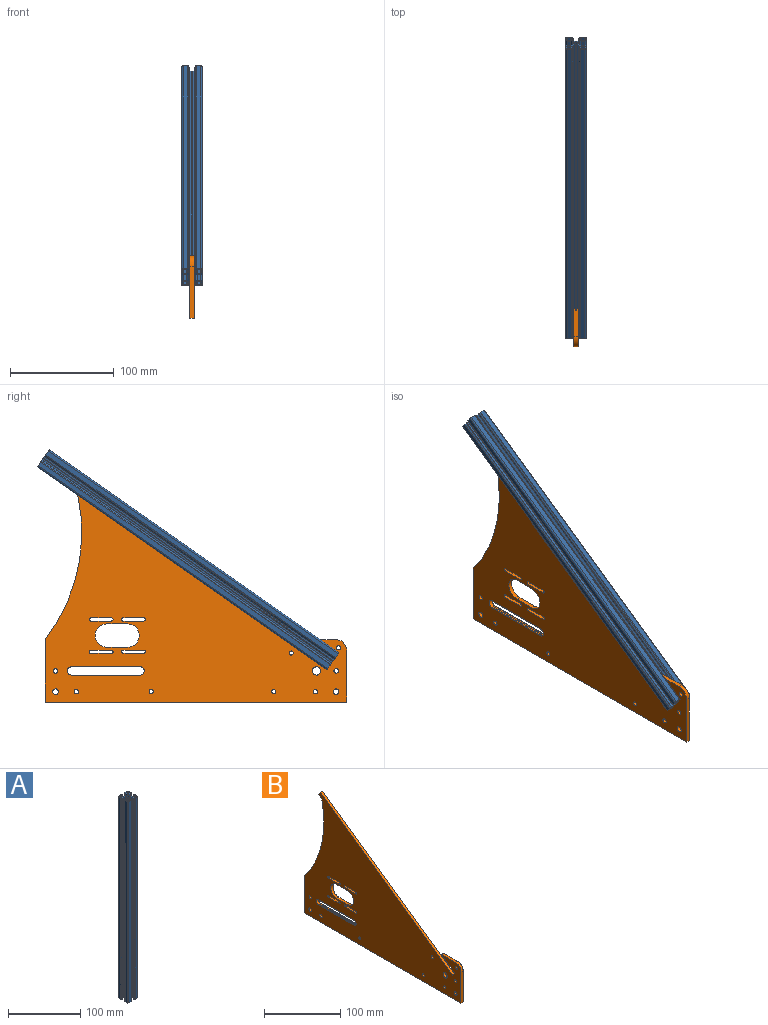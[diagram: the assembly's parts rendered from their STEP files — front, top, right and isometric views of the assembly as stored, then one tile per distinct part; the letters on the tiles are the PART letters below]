
ASSEMBLY  parts=2 mates=1
PART A: 111 faces, bbox 20x20x340 mm
  f0: cylinder r=0.2mm len=340mm, axis (0,0,-1), area 156.7mm2, adj f1,f103,f109,f110
  f1: plane 340x1.28mm, normal (0.71,-0.71,0), area 616.7mm2, adj f0,f2,f109,f110
  f2: cylinder r=0.79mm len=340mm, axis (0,0,-1), area 211mm2, adj f1,f3,f109,f110
  f3: plane 340x4.33mm, normal (1,0,0), area 1472.6mm2, adj f2,f4,f109,f110
  f4: cylinder r=1.5mm len=340mm, axis (0,0,-1), area 741.8mm2, adj f3,f5,f109,f110
  f5: plane 340x4.56mm, normal (0,1,0), area 1548.9mm2, adj f4,f6,f109,f110
  f6: cylinder r=0.8mm len=340mm, axis (0,0,-1), area 213.6mm2, adj f5,f7,f109,f110
  f7: plane 340x1.1mm, normal (-0.71,0.71,0), area 530.8mm2, adj f6,f8,f109,f110
  f8: cylinder r=0.25mm len=340mm, axis (0,0,-1), area 200.3mm2, adj f7,f9,f109,f110
  f9: plane 340x1.05mm, normal (0,-1,0), area 357mm2, adj f8,f10,f109,f110
  f10: plane 340x3.2mm, normal (-1,0,0), area 1088mm2, adj f9,f11,f109,f110
  f11: plane 340x1.6mm, normal (-0.71,0.71,0), area 768mm2, adj f10,f12,f109,f110
  f12: plane 340x1.71mm, normal (0,1,0), area 579.8mm2, adj f11,f13,f109,f110
  f13: plane 340x0.3mm, normal (-0.65,0.76,0), area 135mm2, adj f12,f14,f109,f110
  f14: plane 340x0.3mm, normal (0.65,0.76,0), area 135mm2, adj f13,f15,f109,f110
  f15: plane 340x1.71mm, normal (0,1,0), area 579.8mm2, adj f14,f16,f109,f110
  f16: plane 340x1.6mm, normal (0.71,0.71,0), area 768mm2, adj f15,f17,f109,f110
  f17: plane 340x3.2mm, normal (1,0,0), area 1088mm2, adj f16,f18,f109,f110
  f18: plane 340x1.05mm, normal (0,-1,0), area 357mm2, adj f17,f19,f109,f110
  f19: cylinder r=0.25mm len=340mm, axis (0,0,-1), area 200.3mm2, adj f18,f20,f109,f110
  f20: plane 340x1.1mm, normal (0.71,0.71,0), area 530.8mm2, adj f19,f21,f109,f110
  f21: cylinder r=0.8mm len=340mm, axis (0,0,-1), area 213.6mm2, adj f20,f22,f109,f110
  f22: plane 340x4.56mm, normal (0,1,0), area 1548.9mm2, adj f21,f23,f109,f110
  f23: cylinder r=1.5mm len=340mm, axis (0,0,-1), area 741.8mm2, adj f22,f24,f109,f110
  f24: plane 340x4.33mm, normal (-1,0,0), area 1472.6mm2, adj f23,f25,f109,f110
  f25: cylinder r=0.79mm len=340mm, axis (0,0,-1), area 211mm2, adj f24,f26,f109,f110
  f26: plane 340x1.28mm, normal (-0.71,-0.71,0), area 616.7mm2, adj f25,f27,f109,f110
  f27: cylinder r=0.2mm len=340mm, axis (0,0,-1), area 156.7mm2, adj f26,f28,f109,f110
  f28: plane 340x1.06mm, normal (1,0,0), area 360.5mm2, adj f27,f29,f109,f110
  f29: plane 340x3.12mm, normal (0,-1,0), area 1059.6mm2, adj f28,f30,f109,f110
  f30: plane 340x1.63mm, normal (-0.71,-0.71,0), area 784.3mm2, adj f29,f31,f109,f110
  f31: plane 340x1.59mm, normal (-1,0,0), area 539mm2, adj f30,f32,f109,f110
  f32: plane 340x0.38mm, normal (-0.71,-0.71,0), area 183.1mm2, adj f31,f33,f109,f110
  f33: plane 340x0.38mm, normal (-0.71,0.71,0), area 183.1mm2, adj f32,f34,f109,f110
  f34: plane 340x1.59mm, normal (-1,0,0), area 539mm2, adj f33,f35,f109,f110
  f35: plane 340x1.63mm, normal (-0.71,0.71,0), area 784.3mm2, adj f34,f36,f109,f110
  f36: plane 340x3.12mm, normal (0,1,0), area 1059.6mm2, adj f35,f37,f109,f110
  f37: plane 340x1.06mm, normal (1,0,0), area 360.5mm2, adj f36,f38,f109,f110
  f38: cylinder r=0.2mm len=340mm, axis (0,0,-1), area 156.7mm2, adj f37,f39,f109,f110
  f39: plane 340x1.28mm, normal (-0.71,0.71,0), area 616.7mm2, adj f38,f40,f109,f110
  f40: cylinder r=0.79mm len=340mm, axis (0,0,-1), area 211mm2, adj f39,f41,f109,f110
  f41: plane 340x4.33mm, normal (-1,0,0), area 1472.6mm2, adj f40,f42,f109,f110
  f42: cylinder r=1.5mm len=340mm, axis (0,0,-1), area 741.8mm2, adj f41,f43,f109,f110
  f43: plane 340x4.56mm, normal (0,-1,0), area 1548.9mm2, adj f42,f44,f109,f110
  f44: cylinder r=0.8mm len=340mm, axis (0,0,-1), area 213.6mm2, adj f43,f45,f109,f110
  f45: plane 340x1.1mm, normal (0.71,-0.71,0), area 530.8mm2, adj f44,f46,f109,f110
  f46: cylinder r=0.25mm len=340mm, axis (0,0,-1), area 200.3mm2, adj f45,f47,f109,f110
  f47: plane 340x1.05mm, normal (0,1,0), area 357mm2, adj f46,f48,f109,f110
  f48: plane 340x3.2mm, normal (1,0,0), area 1088mm2, adj f47,f49,f109,f110
  f49: plane 340x1.6mm, normal (0.71,-0.71,0), area 768mm2, adj f48,f50,f109,f110
  f50: plane 340x1.71mm, normal (0,-1,0), area 579.8mm2, adj f49,f51,f109,f110
  f51: plane 340x0.3mm, normal (0.65,-0.76,0), area 135mm2, adj f50,f52,f109,f110
  f52: plane 340x0.3mm, normal (-0.65,-0.76,0), area 135mm2, adj f51,f53,f109,f110
  f53: plane 340x1.71mm, normal (0,-1,0), area 579.8mm2, adj f52,f54,f109,f110
  f54: plane 340x1.6mm, normal (-0.71,-0.71,0), area 768mm2, adj f53,f55,f109,f110
  f55: plane 340x3.2mm, normal (-1,0,0), area 1088mm2, adj f54,f56,f109,f110
  f56: plane 340x1.05mm, normal (0,1,0), area 357mm2, adj f55,f57,f109,f110
  f57: cylinder r=0.25mm len=340mm, axis (0,0,-1), area 200.3mm2, adj f56,f58,f109,f110
  f58: plane 340x1.1mm, normal (-0.71,-0.71,0), area 530.8mm2, adj f57,f59,f109,f110
  f59: cylinder r=0.8mm len=340mm, axis (0,0,-1), area 213.6mm2, adj f58,f60,f109,f110
  f60: plane 340x4.56mm, normal (0,-1,0), area 1548.9mm2, adj f59,f61,f109,f110
  f61: cylinder r=1.5mm len=340mm, axis (0,0,-1), area 741.8mm2, adj f60,f62,f109,f110
  f62: plane 340x4.33mm, normal (1,0,0), area 1472.6mm2, adj f61,f63,f109,f110
  f63: cylinder r=0.79mm len=340mm, axis (0,0,-1), area 211mm2, adj f62,f64,f109,f110
  f64: plane 340x1.28mm, normal (0.71,0.71,0), area 616.7mm2, adj f63,f65,f109,f110
  f65: cylinder r=0.2mm len=340mm, axis (0,0,-1), area 156.7mm2, adj f64,f66,f109,f110
  f66: plane 340x1.06mm, normal (-1,0,0), area 360.5mm2, adj f65,f67,f109,f110
  f67: plane 340x3.12mm, normal (0,1,0), area 1059.6mm2, adj f66,f68,f109,f110
  f68: plane 340x1.63mm, normal (0.71,0.71,0), area 784.3mm2, adj f67,f69,f109,f110
  f69: plane 340x1.59mm, normal (1,0,0), area 539mm2, adj f68,f70,f109,f110
  f70: plane 340x0.38mm, normal (0.71,0.71,0), area 183.1mm2, adj f69,f71,f109,f110
  f71: plane 340x0.38mm, normal (0.71,-0.71,0), area 183.1mm2, adj f70,f72,f109,f110
  f72: plane 340x1.59mm, normal (1,0,0), area 539mm2, adj f71,f73,f109,f110
  f73: plane 340x1.63mm, normal (0.71,-0.71,0), area 784.3mm2, adj f72,f74,f109,f110
  f74: plane 340x3.12mm, normal (0,-1,0), area 1059.6mm2, adj f73,f103,f109,f110
  f75: plane 340x3mm, normal (0,1,0), area 1020mm2, adj f76,f104,f109,f110
  f76: cylinder r=0.5mm len=340mm, axis (0,0,-1), area 210.5mm2, adj f75,f77,f109,f110
  f77: plane 340x3mm, normal (1,0,0), area 1020mm2, adj f76,f78,f109,f110
  f78: cylinder r=0.5mm len=340mm, axis (0,0,-1), area 269.3mm2, adj f77,f79,f109,f110
  f79: plane 340x3mm, normal (0,-1,0), area 1020mm2, adj f78,f80,f109,f110
  f80: cylinder r=0.5mm len=340mm, axis (0,0,-1), area 331.1mm2, adj f79,f81,f109,f110
  f81: plane 340x3mm, normal (-1,0,0), area 1020mm2, adj f80,f104,f109,f110
  f82: plane 340x3mm, normal (0,1,0), area 1020mm2, adj f83,f105,f109,f110
  f83: cylinder r=0.5mm len=340mm, axis (0,0,-1), area 331.1mm2, adj f82,f84,f109,f110
  f84: plane 340x3mm, normal (1,0,0), area 1020mm2, adj f83,f85,f109,f110
  f85: cylinder r=0.5mm len=340mm, axis (0,0,-1), area 278.6mm2, adj f84,f86,f109,f110
  f86: plane 340x3mm, normal (0,-1,0), area 1020mm2, adj f85,f87,f109,f110
  f87: cylinder r=0.5mm len=340mm, axis (0,0,-1), area 210.5mm2, adj f86,f88,f109,f110
  f88: plane 340x3mm, normal (-1,0,0), area 1020mm2, adj f87,f105,f109,f110
  f89: cylinder r=0.5mm len=340mm, axis (0,0,-1), area 278.6mm2, adj f90,f106,f109,f110
  f90: plane 340x3mm, normal (1,0,0), area 1020mm2, adj f89,f91,f109,f110
  f91: cylinder r=0.5mm len=340mm, axis (0,0,-1), area 331.1mm2, adj f90,f92,f109,f110
  f92: plane 340x3mm, normal (0,-1,0), area 1020mm2, adj f91,f93,f109,f110
  f93: cylinder r=0.5mm len=340mm, axis (0,0,-1), area 269.3mm2, adj f92,f94,f109,f110
  f94: plane 340x3mm, normal (-1,0,0), area 1020mm2, adj f93,f95,f109,f110
  f95: cylinder r=0.5mm len=340mm, axis (0,0,-1), area 210.5mm2, adj f94,f106,f109,f110
  f96: cylinder r=0.5mm len=340mm, axis (0,0,-1), area 278.6mm2, adj f97,f107,f109,f110
  f97: plane 340x3mm, normal (-1,0,0), area 1020mm2, adj f96,f98,f109,f110
  f98: cylinder r=0.5mm len=340mm, axis (0,0,-1), area 331.1mm2, adj f97,f99,f109,f110
  f99: plane 340x3mm, normal (0,1,0), area 1020mm2, adj f98,f100,f109,f110
  f100: cylinder r=0.5mm len=340mm, axis (0,0,-1), area 269.3mm2, adj f99,f101,f109,f110
  f101: plane 340x3mm, normal (1,0,0), area 1020mm2, adj f100,f102,f109,f110
  f102: cylinder r=0.5mm len=340mm, axis (0,0,-1), area 210.5mm2, adj f101,f107,f109,f110
  f103: plane 340x1.06mm, normal (-1,0,0), area 360.5mm2, adj f0,f74,f109,f110
  f104: cylinder r=0.5mm len=340mm, axis (0,0,-1), area 278.6mm2, adj f75,f81,f109,f110
  f105: cylinder r=0.5mm len=340mm, axis (0,0,-1), area 269.3mm2, adj f82,f88,f109,f110
  f106: plane 340x3mm, normal (0,1,0), area 1020mm2, adj f89,f95,f109,f110
  f107: plane 340x3mm, normal (0,-1,0), area 1020mm2, adj f96,f102,f109,f110
  f108: cylinder r=2.1mm len=340mm, axis (0,0,-1), area 4486.2mm2, adj f109,f110
  f109: plane 20x20mm, normal (0,0,1), area 150.7mm2, adj f0,f1,f2,f3,f4,f5,f6,f7
  f110: plane 20x20mm, normal (0,0,-1), area 150.7mm2, adj f0,f1,f2,f3,f4,f5,f6,f7
PART B: 176 faces, bbox 4x290x208.7 mm
  f0: cylinder r=1.5mm len=4mm, axis (1,0,0), area 18.8mm2, adj f1,f156,f173,f174
  f1: plane 20x4mm, normal (0,0,-1), area 80mm2, adj f0,f2,f173,f174
  f2: cylinder r=1.5mm len=4mm, axis (1,0,0), area 18.8mm2, adj f1,f156,f173,f174
  f3: plane 20x4mm, normal (0,0,-1), area 80mm2, adj f4,f157,f173,f174
  f4: cylinder r=1.5mm len=4mm, axis (1,0,0), area 18.8mm2, adj f3,f5,f173,f174
  f5: plane 20x4mm, normal (0,0,1), area 80mm2, adj f4,f157,f173,f174
  f6: plane 19.99x4mm, normal (0,0,-1), area 80mm2, adj f7,f158,f173,f174
  f7: cylinder r=1.5mm len=4mm, axis (1,0,0), area 18.8mm2, adj f6,f8,f173,f174
  f8: plane 19.99x4mm, normal (0,0,1), area 80mm2, adj f7,f158,f173,f174
  f9: plane 20x4mm, normal (0,0,-1), area 80mm2, adj f10,f159,f173,f174
  f10: cylinder r=11.2mm len=22.4mm, axis (1,0,0), area 140.7mm2, adj f9,f11,f173,f174
  f11: plane 20x4mm, normal (0,0,1), area 80mm2, adj f10,f159,f173,f174
  f12: cylinder r=1.5mm len=4mm, axis (1,0,0), area 18.9mm2, adj f13,f160,f173,f174
  f13: plane 19.99x4mm, normal (0,0,-1), area 80mm2, adj f12,f14,f173,f174
  f14: cylinder r=1.5mm len=4mm, axis (1,0,0), area 18.8mm2, adj f13,f160,f173,f174
  f15: cylinder r=4mm len=8mm, axis (1,0,0), area 54.3mm2, adj f16,f164,f173,f174
  f16: cylinder r=4mm len=4mm, axis (1,0,0), area 4mm2, adj f15,f17,f173,f174
  f17: cylinder r=4mm len=4mm, axis (1,0,0), area 4mm2, adj f16,f18,f173,f174
  f18: cylinder r=4mm len=4mm, axis (1,0,0), area 4mm2, adj f17,f19,f173,f174
  f19: cylinder r=4mm len=4mm, axis (1,0,0), area 4mm2, adj f18,f20,f173,f174
  f20: cylinder r=4mm len=4mm, axis (1,0,0), area 4mm2, adj f19,f21,f173,f174
  f21: cylinder r=4mm len=4mm, axis (1,0,0), area 4mm2, adj f20,f22,f173,f174
  f22: cylinder r=4mm len=4mm, axis (1,0,0), area 4mm2, adj f21,f23,f173,f174
  f23: cylinder r=4mm len=4mm, axis (1,0,0), area 4mm2, adj f22,f24,f173,f174
  f24: cylinder r=4mm len=4mm, axis (1,0,0), area 4mm2, adj f23,f25,f173,f174
  f25: cylinder r=4mm len=4mm, axis (1,0,0), area 4mm2, adj f24,f26,f173,f174
  f26: cylinder r=4mm len=4mm, axis (1,0,0), area 4mm2, adj f25,f27,f173,f174
  f27: cylinder r=4mm len=4mm, axis (1,0,0), area 4mm2, adj f26,f28,f173,f174
  f28: cylinder r=4mm len=4mm, axis (1,0,0), area 4mm2, adj f27,f29,f173,f174
  f29: cylinder r=4mm len=4mm, axis (1,0,0), area 4mm2, adj f28,f30,f173,f174
  f30: cylinder r=4mm len=4mm, axis (1,0,0), area 4mm2, adj f29,f31,f173,f174
  f31: cylinder r=4mm len=4mm, axis (1,0,0), area 4mm2, adj f30,f32,f173,f174
  f32: cylinder r=4mm len=4mm, axis (1,0,0), area 4mm2, adj f31,f33,f173,f174
  f33: cylinder r=4mm len=4mm, axis (1,0,0), area 4mm2, adj f32,f34,f173,f174
  f34: cylinder r=4mm len=4mm, axis (1,0,0), area 4mm2, adj f33,f35,f173,f174
  f35: cylinder r=4mm len=4mm, axis (1,0,0), area 4mm2, adj f34,f36,f173,f174
  f36: cylinder r=4mm len=4mm, axis (1,0,0), area 4mm2, adj f35,f37,f173,f174
  f37: cylinder r=4mm len=4mm, axis (1,0,0), area 4mm2, adj f36,f38,f173,f174
  f38: cylinder r=4mm len=4mm, axis (1,0,0), area 4mm2, adj f37,f39,f173,f174
  f39: cylinder r=4mm len=4mm, axis (1,0,0), area 4mm2, adj f38,f40,f173,f174
  f40: cylinder r=4mm len=4mm, axis (1,0,0), area 4mm2, adj f39,f41,f173,f174
  f41: cylinder r=4mm len=4mm, axis (1,0,0), area 4mm2, adj f40,f42,f173,f174
  f42: cylinder r=4mm len=4mm, axis (1,0,0), area 4mm2, adj f41,f43,f173,f174
  f43: cylinder r=4mm len=4mm, axis (1,0,0), area 4mm2, adj f42,f44,f173,f174
  f44: cylinder r=4mm len=4mm, axis (1,0,0), area 4mm2, adj f43,f45,f173,f174
  f45: cylinder r=4mm len=4mm, axis (1,0,0), area 4mm2, adj f44,f46,f173,f174
  f46: cylinder r=4mm len=4mm, axis (1,0,0), area 4mm2, adj f45,f47,f173,f174
  f47: cylinder r=4mm len=4mm, axis (1,0,0), area 4mm2, adj f46,f48,f173,f174
  f48: cylinder r=4mm len=4mm, axis (1,0,0), area 4mm2, adj f47,f49,f173,f174
  f49: cylinder r=4mm len=4mm, axis (1,0,0), area 4mm2, adj f48,f50,f173,f174
  f50: cylinder r=4mm len=4mm, axis (1,0,0), area 4mm2, adj f49,f51,f173,f174
  f51: cylinder r=4mm len=4mm, axis (1,0,0), area 4mm2, adj f50,f52,f173,f174
  f52: cylinder r=4mm len=4mm, axis (1,0,0), area 4mm2, adj f51,f53,f173,f174
  f53: cylinder r=4mm len=4mm, axis (1,0,0), area 4mm2, adj f52,f54,f173,f174
  f54: cylinder r=4mm len=4mm, axis (1,0,0), area 4mm2, adj f53,f55,f173,f174
  f55: cylinder r=4mm len=4mm, axis (1,0,0), area 4mm2, adj f54,f56,f173,f174
  f56: cylinder r=4mm len=4mm, axis (1,0,0), area 4mm2, adj f55,f57,f173,f174
  f57: cylinder r=4mm len=4mm, axis (1,0,0), area 4mm2, adj f56,f58,f173,f174
  f58: cylinder r=4mm len=4mm, axis (1,0,0), area 4mm2, adj f57,f59,f173,f174
  f59: cylinder r=4mm len=4mm, axis (1,0,0), area 4mm2, adj f58,f60,f173,f174
  f60: cylinder r=4mm len=4mm, axis (1,0,0), area 4mm2, adj f59,f61,f173,f174
  f61: cylinder r=4mm len=4mm, axis (1,0,0), area 4mm2, adj f60,f62,f173,f174
  f62: cylinder r=4mm len=4mm, axis (1,0,0), area 4mm2, adj f61,f63,f173,f174
  f63: cylinder r=4mm len=4mm, axis (1,0,0), area 4mm2, adj f62,f64,f173,f174
  f64: cylinder r=4mm len=4mm, axis (1,0,0), area 4mm2, adj f63,f65,f173,f174
  f65: cylinder r=4mm len=4mm, axis (1,0,0), area 4mm2, adj f64,f66,f173,f174
  f66: cylinder r=4mm len=4mm, axis (1,0,0), area 4mm2, adj f65,f67,f173,f174
  f67: cylinder r=4mm len=4mm, axis (1,0,0), area 4mm2, adj f66,f68,f173,f174
  f68: cylinder r=4mm len=4mm, axis (1,0,0), area 4mm2, adj f67,f69,f173,f174
  f69: cylinder r=4mm len=4mm, axis (1,0,0), area 4mm2, adj f68,f70,f173,f174
  f70: cylinder r=4mm len=4mm, axis (1,0,0), area 4mm2, adj f69,f71,f173,f174
  f71: cylinder r=4mm len=4mm, axis (1,0,0), area 4mm2, adj f70,f72,f173,f174
  f72: cylinder r=4mm len=4mm, axis (1,0,0), area 4mm2, adj f71,f73,f173,f174
  f73: cylinder r=4mm len=4mm, axis (1,0,0), area 4mm2, adj f72,f74,f173,f174
  f74: cylinder r=4mm len=4mm, axis (1,0,0), area 4mm2, adj f73,f75,f173,f174
  f75: cylinder r=4mm len=4mm, axis (1,0,0), area 4mm2, adj f74,f76,f173,f174
  f76: cylinder r=4mm len=4mm, axis (1,0,0), area 4mm2, adj f75,f77,f173,f174
  f77: cylinder r=4mm len=4mm, axis (1,0,0), area 4mm2, adj f76,f78,f173,f174
  f78: cylinder r=4mm len=4mm, axis (1,0,0), area 4mm2, adj f77,f79,f173,f174
  f79: cylinder r=4mm len=4mm, axis (1,0,0), area 4mm2, adj f78,f80,f173,f174
  f80: cylinder r=4mm len=4mm, axis (1,0,0), area 4mm2, adj f79,f81,f173,f174
  f81: cylinder r=4mm len=8mm, axis (1,0,0), area 54.3mm2, adj f80,f82,f173,f174
  f82: cylinder r=4mm len=4mm, axis (1,0,0), area 4mm2, adj f81,f83,f173,f174
  f83: cylinder r=4mm len=4mm, axis (1,0,0), area 4mm2, adj f82,f84,f173,f174
  f84: cylinder r=4mm len=4mm, axis (1,0,0), area 4mm2, adj f83,f85,f173,f174
  f85: cylinder r=4mm len=4mm, axis (1,0,0), area 4mm2, adj f84,f86,f173,f174
  f86: cylinder r=4mm len=4mm, axis (1,0,0), area 4mm2, adj f85,f87,f173,f174
  f87: cylinder r=4mm len=4mm, axis (1,0,0), area 4mm2, adj f86,f88,f173,f174
  f88: cylinder r=4mm len=4mm, axis (1,0,0), area 4mm2, adj f87,f89,f173,f174
  f89: cylinder r=4mm len=4mm, axis (1,0,0), area 4mm2, adj f88,f90,f173,f174
  f90: cylinder r=4mm len=4mm, axis (1,0,0), area 4mm2, adj f89,f91,f173,f174
  f91: cylinder r=4mm len=4mm, axis (1,0,0), area 4mm2, adj f90,f92,f173,f174
  f92: cylinder r=4mm len=4mm, axis (1,0,0), area 4mm2, adj f91,f93,f173,f174
  f93: cylinder r=4mm len=4mm, axis (1,0,0), area 4mm2, adj f92,f94,f173,f174
  f94: cylinder r=4mm len=4mm, axis (1,0,0), area 4mm2, adj f93,f95,f173,f174
  f95: cylinder r=4mm len=4mm, axis (1,0,0), area 4mm2, adj f94,f96,f173,f174
  f96: cylinder r=4mm len=4mm, axis (1,0,0), area 4mm2, adj f95,f97,f173,f174
  f97: cylinder r=4mm len=4mm, axis (1,0,0), area 4mm2, adj f96,f98,f173,f174
  f98: cylinder r=4mm len=4mm, axis (1,0,0), area 4mm2, adj f97,f99,f173,f174
  f99: cylinder r=4mm len=4mm, axis (1,0,0), area 4mm2, adj f98,f100,f173,f174
  f100: cylinder r=4mm len=4mm, axis (1,0,0), area 4mm2, adj f99,f101,f173,f174
  f101: cylinder r=4mm len=4mm, axis (1,0,0), area 4mm2, adj f100,f102,f173,f174
  f102: cylinder r=4mm len=4mm, axis (1,0,0), area 4mm2, adj f101,f103,f173,f174
  f103: cylinder r=4mm len=4mm, axis (1,0,0), area 4mm2, adj f102,f104,f173,f174
  f104: cylinder r=4mm len=4mm, axis (1,0,0), area 4mm2, adj f103,f105,f173,f174
  f105: cylinder r=4mm len=4mm, axis (1,0,0), area 4mm2, adj f104,f106,f173,f174
  f106: cylinder r=4mm len=4mm, axis (1,0,0), area 4mm2, adj f105,f107,f173,f174
  f107: cylinder r=4mm len=4mm, axis (1,0,0), area 4mm2, adj f106,f108,f173,f174
  f108: cylinder r=4mm len=4mm, axis (1,0,0), area 4mm2, adj f107,f109,f173,f174
  f109: cylinder r=4mm len=4mm, axis (1,0,0), area 4mm2, adj f108,f110,f173,f174
  f110: cylinder r=4mm len=4mm, axis (1,0,0), area 4mm2, adj f109,f111,f173,f174
  f111: cylinder r=4mm len=4mm, axis (1,0,0), area 4mm2, adj f110,f112,f173,f174
  f112: cylinder r=4mm len=4mm, axis (1,0,0), area 4mm2, adj f111,f113,f173,f174
  f113: cylinder r=4mm len=4mm, axis (1,0,0), area 4mm2, adj f112,f114,f173,f174
  f114: cylinder r=4mm len=4mm, axis (1,0,0), area 4mm2, adj f113,f115,f173,f174
  f115: cylinder r=4mm len=4mm, axis (1,0,0), area 4mm2, adj f114,f116,f173,f174
  f116: cylinder r=4mm len=4mm, axis (1,0,0), area 4mm2, adj f115,f117,f173,f174
  f117: cylinder r=4mm len=4mm, axis (1,0,0), area 4mm2, adj f116,f118,f173,f174
  f118: cylinder r=4mm len=4mm, axis (1,0,0), area 4mm2, adj f117,f119,f173,f174
  f119: cylinder r=4mm len=4mm, axis (1,0,0), area 4mm2, adj f118,f120,f173,f174
  f120: cylinder r=4mm len=4mm, axis (1,0,0), area 4mm2, adj f119,f121,f173,f174
  f121: cylinder r=4mm len=4mm, axis (1,0,0), area 4mm2, adj f120,f122,f173,f174
  f122: cylinder r=4mm len=4mm, axis (1,0,0), area 4mm2, adj f121,f123,f173,f174
  f123: cylinder r=4mm len=4mm, axis (1,0,0), area 4mm2, adj f122,f124,f173,f174
  f124: cylinder r=4mm len=4mm, axis (1,0,0), area 4mm2, adj f123,f125,f173,f174
  f125: cylinder r=4mm len=4mm, axis (1,0,0), area 4mm2, adj f124,f126,f173,f174
  f126: cylinder r=4mm len=4mm, axis (1,0,0), area 4mm2, adj f125,f127,f173,f174
  f127: cylinder r=4mm len=4mm, axis (1,0,0), area 4mm2, adj f126,f128,f173,f174
  f128: cylinder r=4mm len=4mm, axis (1,0,0), area 4mm2, adj f127,f129,f173,f174
  f129: cylinder r=4mm len=4mm, axis (1,0,0), area 4mm2, adj f128,f130,f173,f174
  f130: cylinder r=4mm len=4mm, axis (1,0,0), area 4mm2, adj f129,f131,f173,f174
  f131: cylinder r=4mm len=4mm, axis (1,0,0), area 4mm2, adj f130,f132,f173,f174
  f132: cylinder r=4mm len=4mm, axis (1,0,0), area 4mm2, adj f131,f133,f173,f174
  f133: cylinder r=4mm len=4mm, axis (1,0,0), area 4mm2, adj f132,f134,f173,f174
  f134: cylinder r=4mm len=4mm, axis (1,0,0), area 4mm2, adj f133,f135,f173,f174
  f135: cylinder r=4mm len=4mm, axis (1,0,0), area 4mm2, adj f134,f136,f173,f174
  f136: cylinder r=4mm len=4mm, axis (1,0,0), area 4mm2, adj f135,f137,f173,f174
  f137: cylinder r=4mm len=4mm, axis (1,0,0), area 4mm2, adj f136,f138,f173,f174
  f138: cylinder r=4mm len=4mm, axis (1,0,0), area 4mm2, adj f137,f139,f173,f174
  f139: cylinder r=4mm len=4mm, axis (1,0,0), area 4mm2, adj f138,f140,f173,f174
  f140: cylinder r=4mm len=4mm, axis (1,0,0), area 4mm2, adj f139,f141,f173,f174
  f141: cylinder r=4mm len=4mm, axis (1,0,0), area 4mm2, adj f140,f142,f173,f174
  f142: cylinder r=4mm len=4mm, axis (1,0,0), area 4mm2, adj f141,f143,f173,f174
  f143: cylinder r=4mm len=4mm, axis (1,0,0), area 4mm2, adj f142,f144,f173,f174
  f144: cylinder r=4mm len=4mm, axis (1,0,0), area 4mm2, adj f143,f145,f173,f174
  f145: cylinder r=4mm len=4mm, axis (1,0,0), area 4mm2, adj f144,f164,f173,f174
  f146: plane 290x4mm, normal (0,0,-1), area 1160mm2, adj f147,f170,f173,f174
  f147: plane 60x4mm, normal (0,1,0), area 240mm2, adj f146,f148,f173,f174
  f148: cylinder r=168.96mm len=139.02mm, axis (1,0,0), area 588.6mm2, adj f147,f149,f173,f174
  f149: plane 6.13x4.29mm, normal (0,0.57,-0.82), area 29.9mm2, adj f148,f150,f173,f174
  f150: plane 5.35x4mm, normal (0,0.82,0.57), area 26.1mm2, adj f149,f151,f173,f174
  f151: plane 245.78x172.1mm, normal (0,-0.57,0.82), area 1200.2mm2, adj f150,f152,f173,f174
  f152: plane 5.69x4mm, normal (0,0.82,0.57), area 27.8mm2, adj f151,f153,f173,f174
  f153: plane 25.35x17.75mm, normal (0,0.57,-0.82), area 123.8mm2, adj f152,f154,f173,f174
  f154: plane 26.52x4mm, normal (0,0,1), area 106.1mm2, adj f153,f173,f174,f175
  f155: cylinder r=2.15mm len=4.3mm, axis (1,0,0), area 54mm2, adj f173,f174
  f156: plane 20x4mm, normal (0,0,1), area 80mm2, adj f0,f2,f173,f174
  f157: cylinder r=1.5mm len=4mm, axis (1,0,0), area 18.8mm2, adj f3,f5,f173,f174
  f158: cylinder r=1.5mm len=4mm, axis (1,0,0), area 18.9mm2, adj f6,f8,f173,f174
  f159: cylinder r=11.2mm len=22.4mm, axis (1,0,0), area 140.7mm2, adj f9,f11,f173,f174
  f160: plane 19.99x4mm, normal (0,0,1), area 80mm2, adj f12,f14,f173,f174
  f161: cylinder r=2.15mm len=4.3mm, axis (1,0,0), area 54mm2, adj f173,f174
  f162: cylinder r=2mm len=4mm, axis (1,0,0), area 50.3mm2, adj f173,f174
  f163: cylinder r=2mm len=4mm, axis (1,0,0), area 50.3mm2, adj f173,f174
  f164: cylinder r=4mm len=4mm, axis (1,0,0), area 4mm2, adj f15,f145,f173,f174
  f165: cylinder r=2.7mm len=5.4mm, axis (1,0,0), area 67.9mm2, adj f173,f174
  f166: cylinder r=2mm len=4mm, axis (1,0,0), area 50.3mm2, adj f173,f174
  f167: cylinder r=2.15mm len=4.3mm, axis (1,0,0), area 54mm2, adj f173,f174
  f168: cylinder r=2.15mm len=4.3mm, axis (1,0,0), area 54mm2, adj f173,f174
  f169: cylinder r=2mm len=4mm, axis (1,0,0), area 50.3mm2, adj f173,f174
  f170: plane 50x4mm, normal (0,-1,0), area 200mm2, adj f146,f173,f174,f175
  f171: cylinder r=4mm len=8mm, axis (1,0,0), area 100.5mm2, adj f173,f174
  f172: cylinder r=2.7mm len=5.4mm, axis (1,0,0), area 67.9mm2, adj f173,f174
  f173: plane 290x208.66mm, normal (-1,0,0), area 31374.7mm2, adj f0,f1,f2,f3,f4,f5,f6,f7
  f174: plane 290x208.66mm, normal (1,0,0), area 31374.7mm2, adj f0,f1,f2,f3,f4,f5,f6,f7
  f175: cylinder r=10mm len=10mm, axis (1,0,0), area 62.8mm2, adj f154,f170,f173,f174
PLACE A rot(axis=(1,0,0),125deg) t=(-72.55,49.9,59.53)mm
PLACE B t=(-296.55,-103.34,-144.89)mm
MATE fastened A.f108 <-> B.f152  axis (0,0.82,0.57) through (-298.55,-228.61,-135.48)mm
